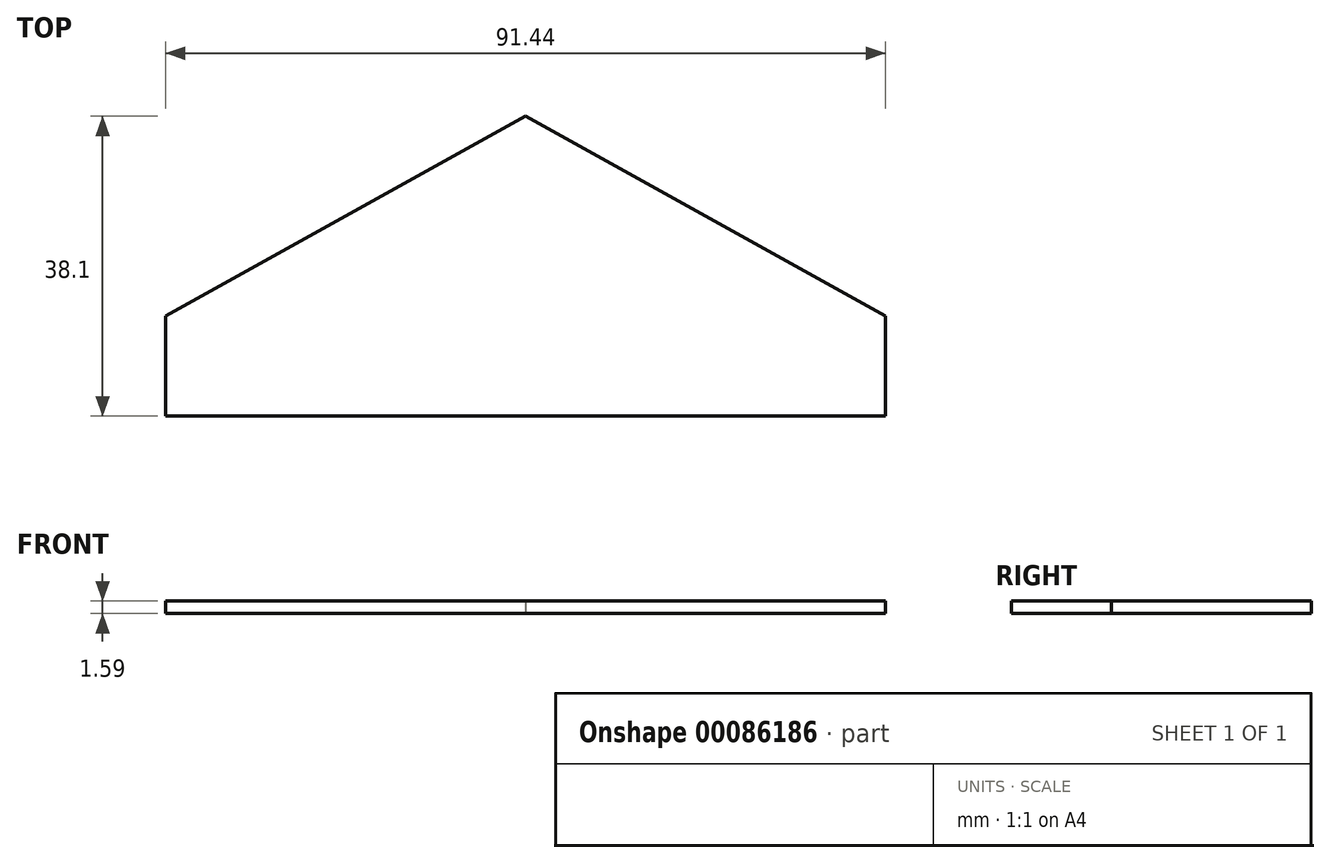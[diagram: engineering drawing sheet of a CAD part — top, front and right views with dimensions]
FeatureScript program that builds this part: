
annotation { "Feature Type Name" : "Feature", "Feature Type Description" : "" }
export const myFeature = defineFeature(function(context is Context, id is Id, definition is map)
    precondition{}
    {
        {
            var Q0;
            Q0=qCreatedBy(makeId("Top.planeOp"),FACE);
            var sketch = newSketch(context, id + "F0", { "sketchPlane" : qUnion([Q0])});
            skLineSegment(sketch, "E0", {"start": v(0, 0) * mm, "end": v(45.72, 0) * mm});
            skLineSegment(sketch, "E1", {"start": v(0, 0) * mm, "end": v(-45.72, 0) * mm});
            skLineSegment(sketch, "E2", {"start": v(0, 0) * mm, "end": v(0, 25.4) * mm});
            skLineSegment(sketch, "E3", {"start": v(0, 25.4) * mm, "end": v(-45.72, 0) * mm});
            skLineSegment(sketch, "E4", {"start": v(0, 25.4) * mm, "end": v(45.72, 0) * mm});
            skLineSegment(sketch, "E5", {"start": v(-45.72, 0) * mm, "end": v(-45.72, -12.7) * mm});
            skLineSegment(sketch, "E6", {"start": v(45.72, 0) * mm, "end": v(45.72, -12.7) * mm});
            skLineSegment(sketch, "E7", {"start": v(-45.72, -12.7) * mm, "end": v(45.72, -12.7) * mm});
            skSolve(sketch);
        }
        {
            var Q0;
            Q0 = qSketchRegion(id + "F0", true);
            extrude(context, id + "F1", {"entities" : qUnion([Q0]), "depth" : 1.59 * mm});
        }
    });
